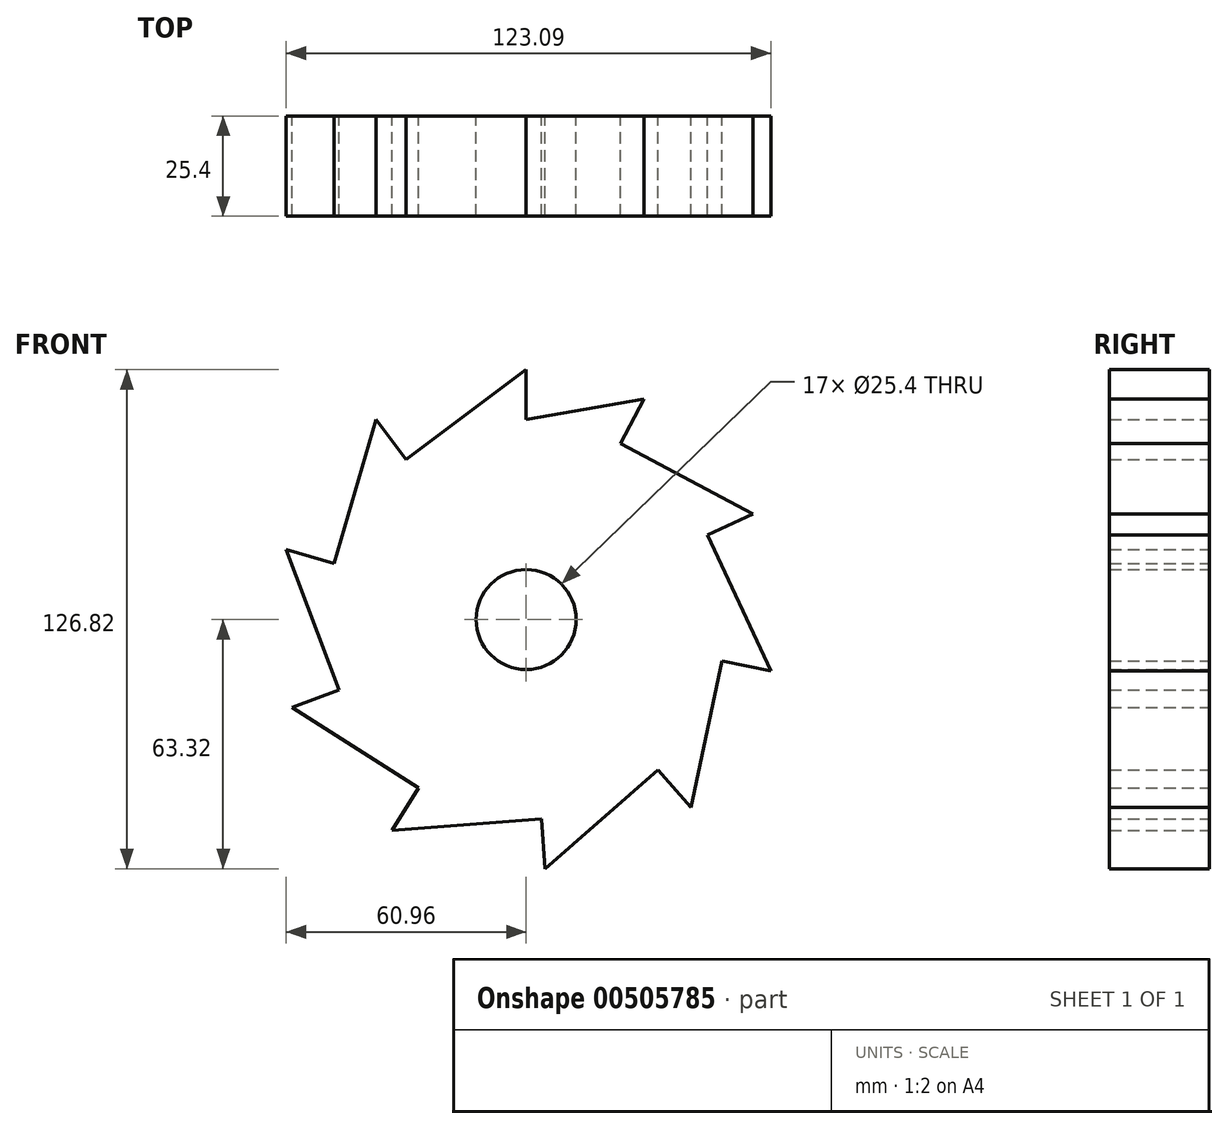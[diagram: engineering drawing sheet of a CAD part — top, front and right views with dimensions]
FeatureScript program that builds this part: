
annotation { "Feature Type Name" : "Feature", "Feature Type Description" : "" }
export const myFeature = defineFeature(function(context is Context, id is Id, definition is map)
    precondition{}
    {
        {
            var Q0;
            Q0=qCreatedBy(makeId("Front.planeOp"),FACE);
            var sketch = newSketch(context, id + "F0", { "sketchPlane" : qUnion([Q0])});
            skCircle(sketch, "E0", {"center": v(0, 0) * mm, "radius": 50.8 * mm});
            skLineSegment(sketch, "E1", {"start": v(0, 50.8) * mm, "end": v(0, 63.5) * mm});
            skLineSegment(sketch, "E2", {"start": v(0, 63.5) * mm, "end": v(-30.48, 40.64) * mm});
            skLineSegment(sketch, "E3", {"start": v(-30.48, 40.64) * mm, "end": v(-38.1, 50.8) * mm});
            skLineSegment(sketch, "E4", {"start": v(-38.1, 50.8) * mm, "end": v(-48.77, 14.22) * mm});
            skLineSegment(sketch, "E5", {"start": v(-48.77, 14.22) * mm, "end": v(-60.96, 17.78) * mm});
            skLineSegment(sketch, "E6", {"start": v(-60.96, 17.78) * mm, "end": v(-47.55, -17.88) * mm});
            skLineSegment(sketch, "E7", {"start": v(-47.55, -17.88) * mm, "end": v(-59.44, -22.35) * mm});
            skLineSegment(sketch, "E8", {"start": v(-59.44, -22.35) * mm, "end": v(-27.31, -42.83) * mm});
            skLineSegment(sketch, "E9", {"start": v(-27.31, -42.83) * mm, "end": v(-34.14, -53.54) * mm});
            skLineSegment(sketch, "E10", {"start": v(-34.14, -53.54) * mm, "end": v(3.85, -50.65) * mm});
            skLineSegment(sketch, "E11", {"start": v(3.85, -50.65) * mm, "end": v(4.82, -63.32) * mm});
            skLineSegment(sketch, "E12", {"start": v(4.82, -63.32) * mm, "end": v(33.47, -38.21) * mm});
            skLineSegment(sketch, "E13", {"start": v(33.47, -38.21) * mm, "end": v(41.84, -47.76) * mm});
            skLineSegment(sketch, "E14", {"start": v(41.84, -47.76) * mm, "end": v(49.7, -10.48) * mm});
            skLineSegment(sketch, "E15", {"start": v(49.7, -10.48) * mm, "end": v(62.13, -13.1) * mm});
            skLineSegment(sketch, "E16", {"start": v(62.13, -13.1) * mm, "end": v(46.06, 21.44) * mm});
            skLineSegment(sketch, "E17", {"start": v(46.06, 21.44) * mm, "end": v(57.57, 26.8) * mm});
            skLineSegment(sketch, "E18", {"start": v(57.57, 26.8) * mm, "end": v(23.98, 44.78) * mm});
            skLineSegment(sketch, "E19", {"start": v(23.98, 44.78) * mm, "end": v(29.98, 55.98) * mm});
            skLineSegment(sketch, "E20", {"start": v(29.98, 55.98) * mm, "end": v(0, 50.8) * mm});
            skCircle(sketch, "E21", {"center": v(0, 0) * mm, "radius": 12.7 * mm});
            skSolve(sketch);
        }
        {
            var Q0;
            Q0=makeQuery(id+"F0.imprint","IMPRINT",FACE,{"disambiguationData":[TD([[makeQuery(id+"F0.imprint","IMPRINT",EDGE,{"derivedFrom":sQuery(id+"F0.wireOp",EDGE,"E21")}),-1.0]])]});
            var Q1;
            {var subQ0=sQuery(id+"F0.wireOp",EDGE,"E1");Q1=makeQuery(id+"F0.imprint","IMPRINT",FACE,{"disambiguationData":[TD([[makeQuery(id+"F0.imprint","IMPRINT",EDGE,{"derivedFrom":subQ0}),1.0]])]});}
            var Q2;
            {var subQ0=sQuery(id+"F0.wireOp",EDGE,"E3");Q2=makeQuery(id+"F0.imprint","IMPRINT",FACE,{"disambiguationData":[TD([[makeQuery(id+"F0.imprint","IMPRINT",EDGE,{"derivedFrom":subQ0}),1.0]])]});}
            var Q3;
            {var subQ0=sQuery(id+"F0.wireOp",EDGE,"E5");Q3=makeQuery(id+"F0.imprint","IMPRINT",FACE,{"disambiguationData":[TD([[makeQuery(id+"F0.imprint","IMPRINT",EDGE,{"derivedFrom":subQ0}),1.0]])]});}
            var Q4;
            {var subQ0=sQuery(id+"F0.wireOp",EDGE,"E7");Q4=makeQuery(id+"F0.imprint","IMPRINT",FACE,{"disambiguationData":[TD([[makeQuery(id+"F0.imprint","IMPRINT",EDGE,{"derivedFrom":subQ0}),1.0]])]});}
            var Q5;
            {var subQ0=sQuery(id+"F0.wireOp",EDGE,"E9");Q5=makeQuery(id+"F0.imprint","IMPRINT",FACE,{"disambiguationData":[TD([[makeQuery(id+"F0.imprint","IMPRINT",EDGE,{"derivedFrom":subQ0}),1.0]])]});}
            var Q6;
            {var subQ0=sQuery(id+"F0.wireOp",EDGE,"E11");Q6=makeQuery(id+"F0.imprint","IMPRINT",FACE,{"disambiguationData":[TD([[makeQuery(id+"F0.imprint","IMPRINT",EDGE,{"derivedFrom":subQ0}),1.0]])]});}
            var Q7;
            {var subQ0=sQuery(id+"F0.wireOp",EDGE,"E13");Q7=makeQuery(id+"F0.imprint","IMPRINT",FACE,{"disambiguationData":[TD([[makeQuery(id+"F0.imprint","IMPRINT",EDGE,{"derivedFrom":subQ0}),1.0]])]});}
            var Q8;
            {var subQ0=sQuery(id+"F0.wireOp",EDGE,"E17");Q8=makeQuery(id+"F0.imprint","IMPRINT",FACE,{"disambiguationData":[TD([[makeQuery(id+"F0.imprint","IMPRINT",EDGE,{"derivedFrom":subQ0}),1.0]])]});}
            var Q9;
            {var subQ2=sQuery(id+"F0.wireOp",EDGE,"E19");Q9=makeQuery(id+"F0.imprint","IMPRINT",FACE,{"disambiguationData":[TD([[makeQuery(id+"F0.imprint","IMPRINT",EDGE,{"derivedFrom":subQ2}),1.0]])]});}
            var Q10;
            {var subQ0=sQuery(id+"F0.wireOp",EDGE,"E15");Q10=makeQuery(id+"F0.imprint","IMPRINT",FACE,{"disambiguationData":[TD([[makeQuery(id+"F0.imprint","IMPRINT",EDGE,{"derivedFrom":subQ0}),1.0]])]});}
            extrude(context, id + "F1", {"entities" : qUnion([Q0, Q1, Q2, Q3, Q4, Q5, Q6, Q7, Q8, Q9, Q10]), "depth" : 25.4 * mm, "offsetDistance" : 25.4 * mm});
        }
    });
